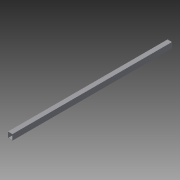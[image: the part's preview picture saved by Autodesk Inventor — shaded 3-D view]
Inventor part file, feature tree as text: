
AUTODESK INVENTOR PART (.ipt)
format: ipt  version: 2015 SP1 (Build 190203100, 203)  size: 78,848 bytes
history: native  units: in
note: dims shown in document units (in); Inventor stores cm internally (conversion verified against a paired STEP export)
features: extrude x1
ambient origin geometry x8: Origin, YZ Plane, XZ Plane, XY Plane, X Axis, Y Axis, Z Axis, Center Point
bodies: Solid1 (feature_tree)
feature tree (1):
  extrude  "Extrusion1"  Depth=1.5748in
